# Revit family: AP-4122m
name_source: partatom
category: Communication Devices
revit_build: Autodesk Revit 2014 (Build: 20130308_1515(x64)
units: mm (PartAtom-declared; Revit-internal decimal feet)

## types (1)
- AP-4122m
    Coverage Horizontal = 90.00°
    Coverage Vertical = 90.00°
    Default Elevation = 0' - 0"
    Depth = 1' - 2 1/2"
    Description = 12-inch, High Power Coaxial Multipurpose Enclosure with 90-degree Conical Coverage
    Height = 1' - 8 3/32"
    Impedance = 4
    Manufacturer = QSC Audio Products, LLC
    Manufacturer URL = www.qscaudio.com
    Model = AP-4122m
    Power Handling = 325
    Product Documentation Link = http://qsc.com
    Product Page URL = http://qsc.com
    SPL Max = 127
    Sensitivity = 96
    URL = http://qsc.com
    Weight Dimensional (kg) = 21.3
    Weight Dimensional (lb) = 46.7
    Weight Product (kg) = 18.1
    Weight Product (lb) = 39.7
    Width = 1' - 3 3/32"

## geometry (parser evidence)
native form markers: Blend x4, Sweep x8
no freeform markers — native parametric forms only
